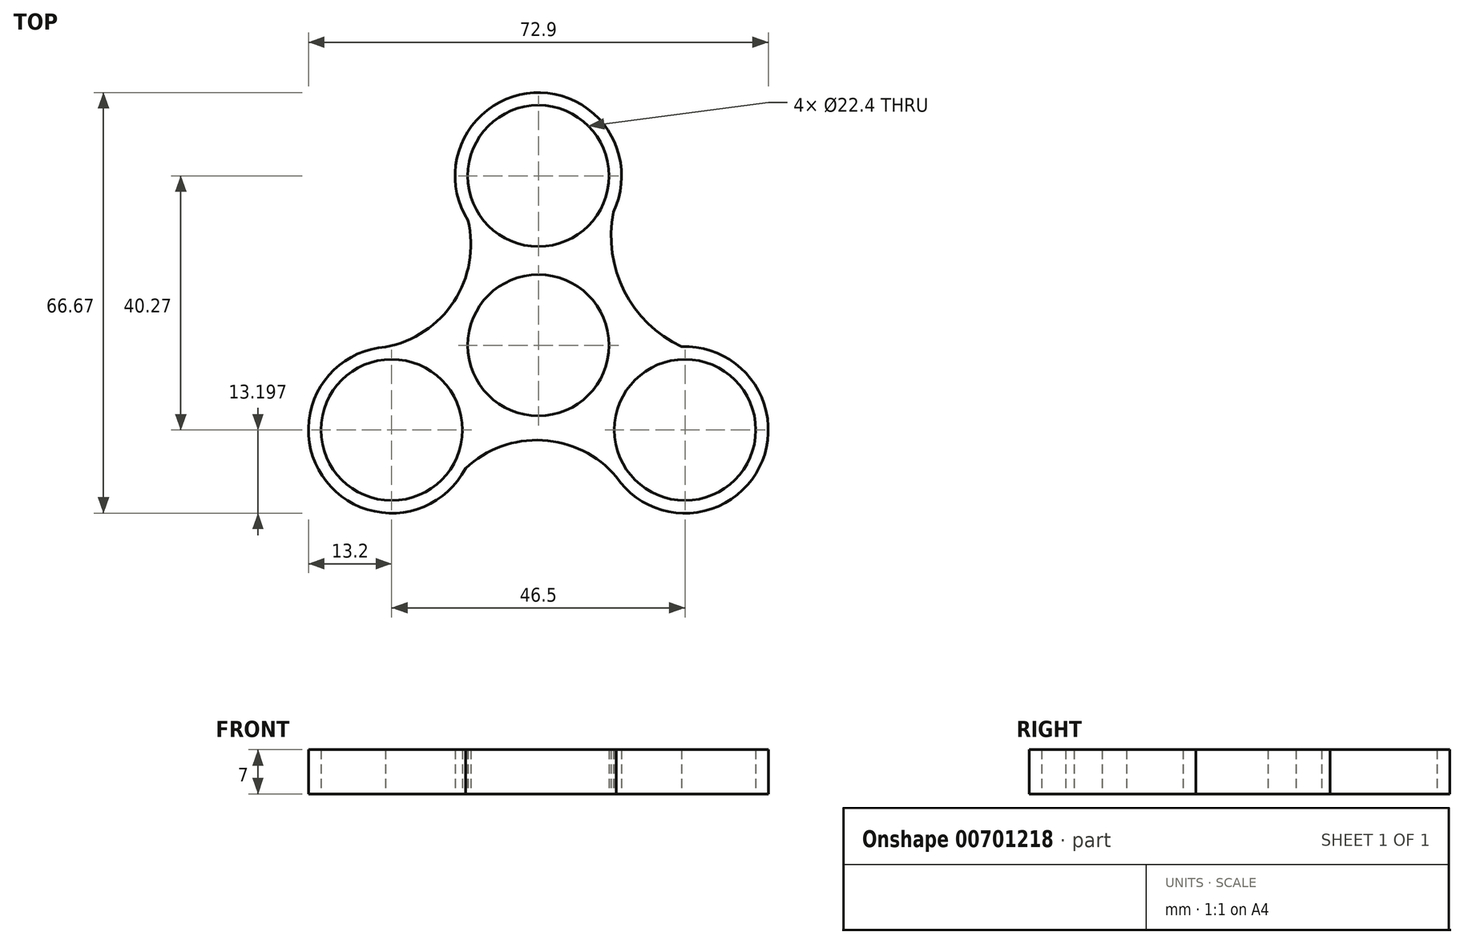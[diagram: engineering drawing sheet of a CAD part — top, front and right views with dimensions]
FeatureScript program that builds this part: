
annotation { "Feature Type Name" : "Feature", "Feature Type Description" : "" }
export const myFeature = defineFeature(function(context is Context, id is Id, definition is map)
    precondition{}
    {
        {
            var Q0;
            Q0=qCreatedBy(makeId("Top.planeOp"),FACE);
            var sketch = newSketch(context, id + "F0", { "sketchPlane" : qUnion([Q0])});
            skCircle(sketch, "E0", {"center": v(0, 0) * mm, "radius": 11.2 * mm});
            skCircle(sketch, "E1", {"center": v(0, 26.85) * mm, "radius": 11.2 * mm});
            skCircle(sketch, "E2.1.0", {"center": v(-23.25, -13.42) * mm, "radius": 11.2 * mm});
            skCircle(sketch, "E2.2.0", {"center": v(23.25, -13.42) * mm, "radius": 11.2 * mm});
            skArc(sketch, "E3", {"start": v(12.33, -20.83) * mm, "mid": v(35.04, -19.36) * mm, "end": v(22.7, -0.24) * mm});
            skArc(sketch, "E4", {"start": v(-24.2, -0.26) * mm, "mid": v(-34.28, -20.67) * mm, "end": v(-11.55, -19.53) * mm});
            skArc(sketch, "E5.1.2", {"start": v(11.88, 21.1) * mm, "mid": v(-0.76, 40.02) * mm, "end": v(-11.14, 19.77) * mm});
            skArc(sketch, "E5.2.1", {"start": v(11.88, 21.1) * mm, "mid": v(-0.76, 40.02) * mm, "end": v(-11.14, 19.77) * mm});
            skPoint(sketch, "E5.center", {"position": v(-3.5, -12.73) * mm});
            skArc(sketch, "E6.1.0", {"start": v(-24.2, -0.26) * mm, "mid": v(-13.38, 6.95) * mm, "end": v(-11.14, 19.77) * mm});
            skArc(sketch, "E6.2.0", {"start": v(12.33, -20.83) * mm, "mid": v(0.67, -15.06) * mm, "end": v(-11.55, -19.53) * mm});
            skLineSegment(sketch, "E7.trimOffspring", {"start": v(9.7, 5.6) * mm, "end": v(13.02, 7.52) * mm, "construction": true});
            skArc(sketch, "E8", {"start": v(11.88, 21.1) * mm, "mid": v(13.63, 8.57) * mm, "end": v(22.7, -0.24) * mm});
            skSolve(sketch);
        }
        {
            var Q0;
            Q0=makeQuery(id+"F0.imprint","IMPRINT",FACE,{"disambiguationData":[TD([[makeQuery(id+"F0.imprint","IMPRINT",EDGE,{"derivedFrom":sQuery(id+"F0.wireOp",EDGE,"E0")}),-1.0]])]});
            extrude(context, id + "F1", {"entities" : qUnion([Q0]), "depth" : 7 * mm, "offsetDistance" : 25 * mm});
        }
    });
